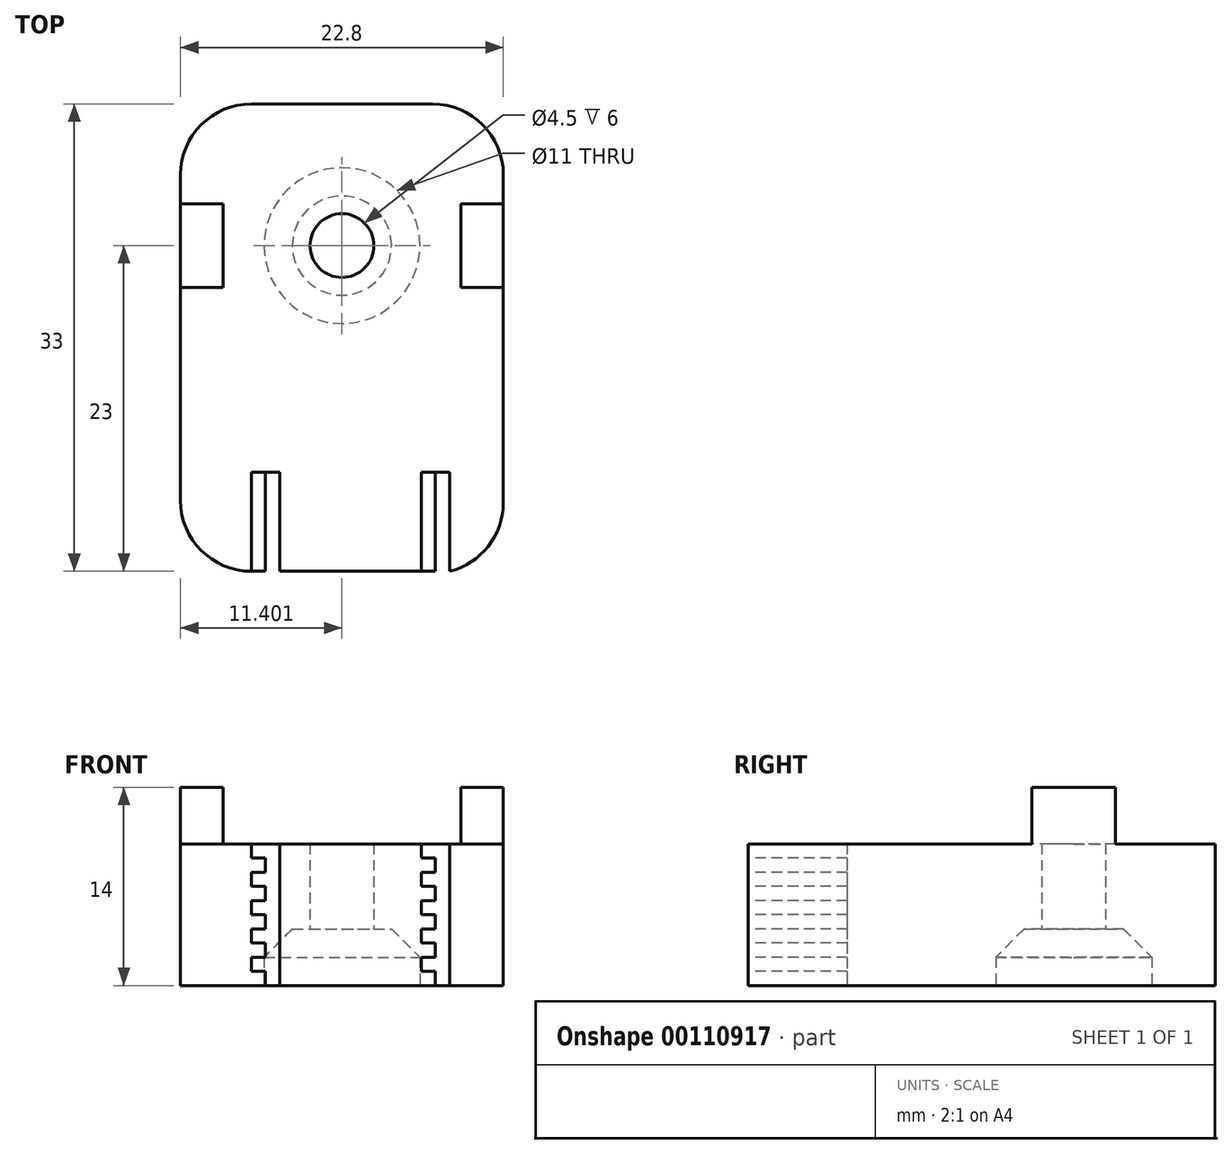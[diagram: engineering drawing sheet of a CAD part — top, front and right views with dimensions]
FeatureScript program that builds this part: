
annotation { "Feature Type Name" : "Feature", "Feature Type Description" : "" }
export const myFeature = defineFeature(function(context is Context, id is Id, definition is map)
    precondition{}
    {
        {
            var Q0;
            Q0=qCreatedBy(makeId("Top.planeOp"),FACE);
            var sketch = newSketch(context, id + "F0", { "sketchPlane" : qUnion([Q0])});
            skLineSegment(sketch, "E0.bottom", {"start": v(-4.06, 0) * mm, "end": v(14.44, 0) * mm});
            skLineSegment(sketch, "E0.top", {"start": v(-4.06, 33) * mm, "end": v(14.44, 33) * mm});
            skLineSegment(sketch, "E0.left", {"start": v(-4.06, 0) * mm, "end": v(-4.06, 33) * mm});
            skLineSegment(sketch, "E0.right", {"start": v(14.44, 0) * mm, "end": v(14.44, 33) * mm});
            skLineSegment(sketch, "E1", {"start": v(-4.06, 13) * mm, "end": v(14.44, 13) * mm});
            skLineSegment(sketch, "E2.bottom", {"start": v(-4.06, 25.95) * mm, "end": v(-1.06, 25.95) * mm});
            skLineSegment(sketch, "E2.top", {"start": v(-4.06, 20.05) * mm, "end": v(-1.06, 20.05) * mm});
            skLineSegment(sketch, "E2.left", {"start": v(-4.06, 25.95) * mm, "end": v(-4.06, 20.05) * mm});
            skLineSegment(sketch, "E2.right", {"start": v(-1.06, 25.95) * mm, "end": v(-1.06, 20.05) * mm});
            skLineSegment(sketch, "E3.bottom", {"start": v(14.44, 25.95) * mm, "end": v(11.44, 25.95) * mm});
            skLineSegment(sketch, "E3.top", {"start": v(14.44, 20.05) * mm, "end": v(11.44, 20.05) * mm});
            skLineSegment(sketch, "E3.left", {"start": v(14.44, 25.95) * mm, "end": v(14.44, 20.05) * mm});
            skLineSegment(sketch, "E3.right", {"start": v(11.44, 25.95) * mm, "end": v(11.44, 20.05) * mm});
            skCircle(sketch, "E4", {"center": v(5.2, 23) * mm, "radius": 2.25 * mm});
            skPoint(sketch, "E5", {"position": v(-1.06, 23) * mm});
            skPoint(sketch, "E6", {"position": v(-4.06, 23) * mm});
            skLineSegment(sketch, "E7", {"start": v(-4.06, 23) * mm, "end": v(14.44, 23) * mm});
            skLineSegment(sketch, "E8.bottom", {"start": v(14.44, 13) * mm, "end": v(18.74, 13) * mm});
            skLineSegment(sketch, "E8.top", {"start": v(14.44, 0) * mm, "end": v(18.74, 0) * mm});
            skLineSegment(sketch, "E8.left", {"start": v(14.44, 13) * mm, "end": v(14.44, 0) * mm});
            skLineSegment(sketch, "E8.right", {"start": v(18.74, 13) * mm, "end": v(18.74, 0) * mm});
            skLineSegment(sketch, "E9.bottom", {"start": v(14.44, 33) * mm, "end": v(18.74, 33) * mm});
            skLineSegment(sketch, "E9.left", {"start": v(14.44, 33) * mm, "end": v(14.44, 13) * mm});
            skLineSegment(sketch, "E9.right", {"start": v(18.74, 33) * mm, "end": v(18.74, 13) * mm});
            skLineSegment(sketch, "E10.bottom", {"start": v(18.74, 25.95) * mm, "end": v(15.74, 25.95) * mm});
            skLineSegment(sketch, "E10.top", {"start": v(18.74, 20.05) * mm, "end": v(15.74, 20.05) * mm});
            skLineSegment(sketch, "E10.left", {"start": v(18.74, 25.95) * mm, "end": v(18.74, 20.05) * mm});
            skLineSegment(sketch, "E10.right", {"start": v(15.74, 25.95) * mm, "end": v(15.74, 20.05) * mm});
            skCircle(sketch, "E11", {"center": v(7.34, 23) * mm, "radius": 2.25 * mm});
            skPoint(sketch, "E12", {"position": v(7.34, 0) * mm});
            skSolve(sketch);
        }
        {
            var Q0;
            {var subQ0=sQuery(id+"F0.wireOp",EDGE,"E0.bottom");Q0=makeQuery(id+"F0.imprint","IMPRINT",FACE,{"disambiguationData":[TD([[makeQuery(id+"F0.imprint","IMPRINT",EDGE,{"derivedFrom":subQ0}),1.0]])]});}
            var Q1;
            Q1=makeQuery(id+"F0.imprint","IMPRINT",FACE,{"disambiguationData":[TD([[makeQuery(id+"F0.imprint","IMPRINT",EDGE,{"derivedFrom":sQuery(id+"F0.wireOp",EDGE,"E8.bottom")}),-1.0]])]});
            var Q2;
            Q2=makeQuery(id+"F0.imprint","IMPRINT",FACE,{"disambiguationData":[TD([[makeQuery(id+"F0.imprint","IMPRINT",EDGE,{"derivedFrom":sQuery(id+"F0.wireOp",EDGE,"E8.top")}),1.0]])]});
            var Q3;
            {var subQ9=sQuery(id+"F0.wireOp",EDGE,"E9.bottom");Q3=makeQuery(id+"F0.imprint","IMPRINT",FACE,{"disambiguationData":[TD([[makeQuery(id+"F0.imprint","IMPRINT",EDGE,{"derivedFrom":subQ9}),-1.0]])]});}
            var Q4;
            {var subQ5=sQuery(id+"F0.wireOp",EDGE,"E1");Q4=makeQuery(id+"F0.imprint","IMPRINT",FACE,{"disambiguationData":[TD([[makeQuery(id+"F0.imprint","IMPRINT",EDGE,{"derivedFrom":subQ5}),1.0]])]});}
            var Q5;
            {var subQ1=sQuery(id+"F0.wireOp",EDGE,"E3.top");Q5=makeQuery(id+"F0.imprint","IMPRINT",FACE,{"disambiguationData":[TD([[makeQuery(id+"F0.imprint","IMPRINT",EDGE,{"derivedFrom":subQ1}),-1.0]])]});}
            var Q6;
            {var subQ6=sQuery(id+"F0.wireOp",EDGE,"E3.bottom");Q6=makeQuery(id+"F0.imprint","IMPRINT",FACE,{"disambiguationData":[TD([[makeQuery(id+"F0.imprint","IMPRINT",EDGE,{"derivedFrom":subQ6}),1.0]])]});}
            var Q7;
            {var subQ5=sQuery(id+"F0.wireOp",EDGE,"E0.top");Q7=makeQuery(id+"F0.imprint","IMPRINT",FACE,{"disambiguationData":[TD([[makeQuery(id+"F0.imprint","IMPRINT",EDGE,{"derivedFrom":subQ5}),-1.0]])]});}
            var Q8;
            {var subQ0=sQuery(id+"F0.wireOp",EDGE,"E7");var subQ1=sQuery(id+"F0.wireOp",EDGE,"E4");var subQ2=makeQuery(id+"F0.imprint","INTERSECT",VERTEX,{"disambiguationData":[OD(1.0)],"derivedFrom":[subQ1,subQ0]});Q8=makeQuery(id+"F0.imprint","IMPRINT",FACE,{"disambiguationData":[TD([[makeQuery(id+"F0.imprint","IMPRINT",EDGE,{"disambiguationData":[TD([[subQ2,-1.0]])],"derivedFrom":subQ1}),1.0]])]});}
            var Q9;
            {var subQ0=sQuery(id+"F0.wireOp",EDGE,"E11");var subQ1=sQuery(id+"F0.wireOp",EDGE,"E4");var subQ2=makeQuery(id+"F0.imprint","INTERSECT",VERTEX,{"disambiguationData":[OD(0.0)],"derivedFrom":[subQ1,subQ0]});Q9=makeQuery(id+"F0.imprint","IMPRINT",FACE,{"disambiguationData":[TD([[makeQuery(id+"F0.imprint","IMPRINT",EDGE,{"disambiguationData":[TD([[subQ2,-1.0]])],"derivedFrom":subQ1}),1.0]])]});}
            extrude(context, id + "F1", {"entities" : qUnion([Q0, Q1, Q2, Q3, Q4, Q5, Q6, Q7, Q8, Q9]), "depth" : 10 * mm});
        }
        {
            var Q0;
            Q0=makeQuery(id+"F1.opExtrude","SWEPT_FACE",FACE,{"disambiguationData":[OSD([sQuery(id+"F0.wireOp",EDGE,"E0.bottom")])]});
            var sketch = newSketch(context, id + "F2", { "sketchPlane" : qUnion([Q0])});
            skLineSegment(sketch, "E13", {"start": v(0.94, 10) * mm, "end": v(0.94, 9) * mm});
            skLineSegment(sketch, "E14", {"start": v(0.94, 9) * mm, "end": v(1.94, 9) * mm});
            skLineSegment(sketch, "E15", {"start": v(1.94, 9) * mm, "end": v(1.94, 8) * mm});
            skLineSegment(sketch, "E16", {"start": v(1.94, 8) * mm, "end": v(0.94, 8) * mm});
            skLineSegment(sketch, "E17", {"start": v(0.94, 8) * mm, "end": v(0.94, 7) * mm});
            skLineSegment(sketch, "E18", {"start": v(0.94, 7) * mm, "end": v(1.94, 7) * mm});
            skLineSegment(sketch, "E19", {"start": v(1.94, 7) * mm, "end": v(1.94, 6) * mm});
            skLineSegment(sketch, "E20", {"start": v(1.94, 6) * mm, "end": v(0.94, 6) * mm});
            skLineSegment(sketch, "E21", {"start": v(0.94, 6) * mm, "end": v(0.94, 5) * mm});
            skLineSegment(sketch, "E22", {"start": v(0.94, 5) * mm, "end": v(1.94, 5) * mm});
            skLineSegment(sketch, "E23", {"start": v(1.94, 5) * mm, "end": v(1.94, 4) * mm});
            skLineSegment(sketch, "E24", {"start": v(1.94, 4) * mm, "end": v(0.94, 4) * mm});
            skLineSegment(sketch, "E25", {"start": v(0.94, 4) * mm, "end": v(0.94, 3) * mm});
            skLineSegment(sketch, "E26", {"start": v(0.94, 3) * mm, "end": v(1.94, 3) * mm});
            skLineSegment(sketch, "E27", {"start": v(1.94, 3) * mm, "end": v(1.94, 2) * mm});
            skLineSegment(sketch, "E28", {"start": v(1.94, 2) * mm, "end": v(0.94, 2) * mm});
            skLineSegment(sketch, "E29", {"start": v(0.94, 2) * mm, "end": v(0.94, 1) * mm});
            skLineSegment(sketch, "E30", {"start": v(0.94, 1) * mm, "end": v(1.94, 1) * mm});
            skLineSegment(sketch, "E31", {"start": v(1.94, 1) * mm, "end": v(1.94, 0) * mm});
            skLineSegment(sketch, "E32", {"start": v(1.94, 0) * mm, "end": v(0.94, 0) * mm});
            skLineSegment(sketch, "E33", {"start": v(2.94, 10) * mm, "end": v(2.94, 0) * mm});
            skLineSegment(sketch, "E34", {"start": v(0.94, 10) * mm, "end": v(2.94, 10) * mm});
            skLineSegment(sketch, "E35", {"start": v(2.94, 0) * mm, "end": v(1.94, 0) * mm});
            skLineSegment(sketch, "E36", {"start": v(12.94, 10) * mm, "end": v(12.94, 9) * mm});
            skLineSegment(sketch, "E37", {"start": v(12.94, 9) * mm, "end": v(13.94, 9) * mm});
            skLineSegment(sketch, "E38", {"start": v(13.94, 9) * mm, "end": v(13.94, 8) * mm});
            skLineSegment(sketch, "E39", {"start": v(13.94, 8) * mm, "end": v(12.94, 8) * mm});
            skLineSegment(sketch, "E40", {"start": v(12.94, 8) * mm, "end": v(12.94, 7) * mm});
            skLineSegment(sketch, "E41", {"start": v(12.94, 7) * mm, "end": v(13.94, 7) * mm});
            skLineSegment(sketch, "E42", {"start": v(13.94, 7) * mm, "end": v(13.94, 6) * mm});
            skLineSegment(sketch, "E43", {"start": v(13.94, 6) * mm, "end": v(12.94, 6) * mm});
            skLineSegment(sketch, "E44", {"start": v(12.94, 6) * mm, "end": v(12.94, 5) * mm});
            skLineSegment(sketch, "E45", {"start": v(12.94, 5) * mm, "end": v(13.94, 5) * mm});
            skLineSegment(sketch, "E46", {"start": v(13.94, 5) * mm, "end": v(13.94, 4) * mm});
            skLineSegment(sketch, "E47", {"start": v(13.94, 4) * mm, "end": v(12.94, 4) * mm});
            skLineSegment(sketch, "E48", {"start": v(12.94, 4) * mm, "end": v(12.94, 3) * mm});
            skLineSegment(sketch, "E49", {"start": v(12.94, 3) * mm, "end": v(13.94, 3) * mm});
            skLineSegment(sketch, "E50", {"start": v(13.94, 3) * mm, "end": v(13.94, 2) * mm});
            skLineSegment(sketch, "E51", {"start": v(13.94, 2) * mm, "end": v(12.94, 2) * mm});
            skLineSegment(sketch, "E52", {"start": v(12.94, 2) * mm, "end": v(12.94, 1) * mm});
            skLineSegment(sketch, "E53", {"start": v(12.94, 1) * mm, "end": v(13.94, 1) * mm});
            skLineSegment(sketch, "E54", {"start": v(13.94, 1) * mm, "end": v(13.94, 0) * mm});
            skLineSegment(sketch, "E55", {"start": v(13.94, 0) * mm, "end": v(12.94, 0) * mm});
            skLineSegment(sketch, "E56", {"start": v(14.94, 10) * mm, "end": v(14.94, 0) * mm});
            skLineSegment(sketch, "E57", {"start": v(12.94, 10) * mm, "end": v(14.94, 10) * mm});
            skLineSegment(sketch, "E58", {"start": v(14.94, 0) * mm, "end": v(13.94, 0) * mm});
            skPoint(sketch, "E59.centerSnap0", {"position": v(-4.06, 5) * mm});
            skPoint(sketch, "E60", {"position": v(7.34, 10) * mm});
            skSolve(sketch);
        }
        {
            var Q0;
            Q0=makeQuery(id+"F2.imprint","IMPRINT",FACE,{"disambiguationData":[TD([[makeQuery(id+"F2.imprint","IMPRINT",EDGE,{"derivedFrom":sQuery(id+"F2.wireOp",EDGE,"E13")}),1.0]])]});
            var Q1;
            Q1=makeQuery(id+"F2.imprint","IMPRINT",FACE,{"disambiguationData":[TD([[makeQuery(id+"F2.imprint","IMPRINT",EDGE,{"derivedFrom":sQuery(id+"F2.wireOp",EDGE,"E36")}),1.0]])]});
            extrude(context, id + "F3", {"entities" : qUnion([Q0, Q1]), "operationType" : NewBodyOperationType.REMOVE, "oppositeDirection" : true, "depth" : 7 * mm});
        }
        {
            var Q0;
            Q0=makeQuery(id+"F1.opExtrude","SWEPT_EDGE",EDGE,{"disambiguationData":[OSD([sQuery(id+"F0.wireOp",EDGE,"E0.top"),sQuery(id+"F0.wireOp",EDGE,"E0.right")])]});
            var Q1;
            Q1=makeQuery(id+"F1.opExtrude","SWEPT_EDGE",EDGE,{"disambiguationData":[OSD([sQuery(id+"F0.wireOp",EDGE,"E0.top"),sQuery(id+"F0.wireOp",EDGE,"E0.left")])]});
            var Q2;
            Q2=makeQuery(id+"F1.opExtrude","SWEPT_EDGE",EDGE,{"disambiguationData":[OSD([sQuery(id+"F0.wireOp",EDGE,"E0.bottom"),sQuery(id+"F0.wireOp",EDGE,"E0.left")])]});
            var Q3;
            Q3=makeQuery(id+"F1.opExtrude","SWEPT_EDGE",EDGE,{"disambiguationData":[OSD([sQuery(id+"F0.wireOp",EDGE,"E0.bottom"),sQuery(id+"F0.wireOp",EDGE,"E0.right")])]});
            var Q4;
            Q4=makeQuery(id+"F1.opExtrude","SWEPT_EDGE",EDGE,{"disambiguationData":[OSD([sQuery(id+"F0.wireOp",EDGE,"E8.top"),sQuery(id+"F0.wireOp",EDGE,"E8.right")])]});
            var Q5;
            Q5=makeQuery(id+"F1.opExtrude","SWEPT_EDGE",EDGE,{"disambiguationData":[OSD([sQuery(id+"F0.wireOp",EDGE,"E8.bottom"),sQuery(id+"F0.wireOp",EDGE,"E8.right")])]});
            var Q6;
            Q6=makeQuery(id+"F1.opExtrude","SWEPT_EDGE",EDGE,{"disambiguationData":[OSD([sQuery(id+"F0.wireOp",EDGE,"E9.bottom"),sQuery(id+"F0.wireOp",EDGE,"E9.right")])]});
            fillet(context, id + "F4", {"entities" : qUnion([Q0, Q1, Q2, Q3, Q4, Q5, Q6]), "radius" : 5 * mm, "tangentPropagation" : true, "allowEdgeOverflow" : false});
        }
        {
            var Q0;
            {var subQ0=sQuery(id+"F0.wireOp",EDGE,"E2.bottom");Q0=makeQuery(id+"F0.imprint","IMPRINT",FACE,{"disambiguationData":[TD([[makeQuery(id+"F0.imprint","IMPRINT",EDGE,{"derivedFrom":subQ0}),-1.0]])]});}
            var Q1;
            {var subQ0=sQuery(id+"F0.wireOp",EDGE,"E2.top");Q1=makeQuery(id+"F0.imprint","IMPRINT",FACE,{"disambiguationData":[TD([[makeQuery(id+"F0.imprint","IMPRINT",EDGE,{"derivedFrom":subQ0}),1.0]])]});}
            var Q2;
            Q2=makeQuery(id+"F0.imprint","IMPRINT",FACE,{"disambiguationData":[TD([[makeQuery(id+"F0.imprint","IMPRINT",EDGE,{"derivedFrom":sQuery(id+"F0.wireOp",EDGE,"E10.bottom")}),1.0]])]});
            extrude(context, id + "F5", {"entities" : qUnion([Q0, Q1, Q2]), "operationType" : NewBodyOperationType.ADD, "depth" : 14 * mm});
        }
        {
            var Q0;
            {var subQ0=sQuery(id+"F0.wireOp",EDGE,"E10.right");var subQ1=sQuery(id+"F0.wireOp",EDGE,"E10.top");var subQ2=sQuery(id+"F0.wireOp",EDGE,"E10.bottom");var subQ3=sQuery(id+"F0.wireOp",EDGE,"E2.right");var subQ4=sQuery(id+"F0.wireOp",EDGE,"E2.top");var subQ5=sQuery(id+"F0.wireOp",EDGE,"E2.bottom");Q0=makeQuery(id+"F5.boolean.opBoolean","MERGE",FACE,{"derivedFrom":[makeQuery(id+"F1.opExtrude","CAP_FACE",FACE,{"disambiguationData":[OSD([sQuery(id+"F0.wireOp",EDGE,"E0.bottom"),sQuery(id+"F0.wireOp",EDGE,"E0.top"),sQuery(id+"F0.wireOp",EDGE,"E0.left"),subQ5,subQ4,subQ3,sQuery(id+"F0.wireOp",EDGE,"E8.top"),sQuery(id+"F0.wireOp",EDGE,"E8.right"),sQuery(id+"F0.wireOp",EDGE,"E9.bottom"),sQuery(id+"F0.wireOp",EDGE,"E9.right"),subQ2,subQ1,subQ0,sQuery(id+"F0.wireOp",EDGE,"E11")])],"isStart":true}),makeQuery(id+"F5.opExtrude","CAP_FACE",FACE,{"disambiguationData":[OSD([subQ5,subQ4,sQuery(id+"F0.wireOp",EDGE,"E2.left"),subQ3])],"isStart":true}),makeQuery(id+"F5.opExtrude","CAP_FACE",FACE,{"disambiguationData":[OSD([subQ2,subQ1,sQuery(id+"F0.wireOp",EDGE,"E10.left"),subQ0])],"isStart":true})]});}
            var sketch = newSketch(context, id + "F6", { "sketchPlane" : qUnion([Q0])});
            skCircle(sketch, "E61", {"center": v(7.34, -23) * mm, "radius": 5.5 * mm});
            skSolve(sketch);
        }
        {
            var Q0;
            Q0 = qSketchRegion(id + "F6", true);
            extrude(context, id + "F7", {"entities" : qUnion([Q0]), "operationType" : NewBodyOperationType.REMOVE, "oppositeDirection" : true, "depth" : 4 * mm});
        }
        {
            var Q0;
            Q0=makeQuery(id+"F7.boolean.opBoolean","COPY",EDGE,{"derivedFrom":makeQuery(id+"F7.opExtrude","CAP_EDGE",EDGE,{"disambiguationData":[OSD([sQuery(id+"F6.wireOp",EDGE,"E61")])],"isStart":false})});
            chamfer(context, id + "F8", {"entities" : qUnion([Q0]), "width" : 2 * mm, "tangentPropagation" : true});
        }
    });
